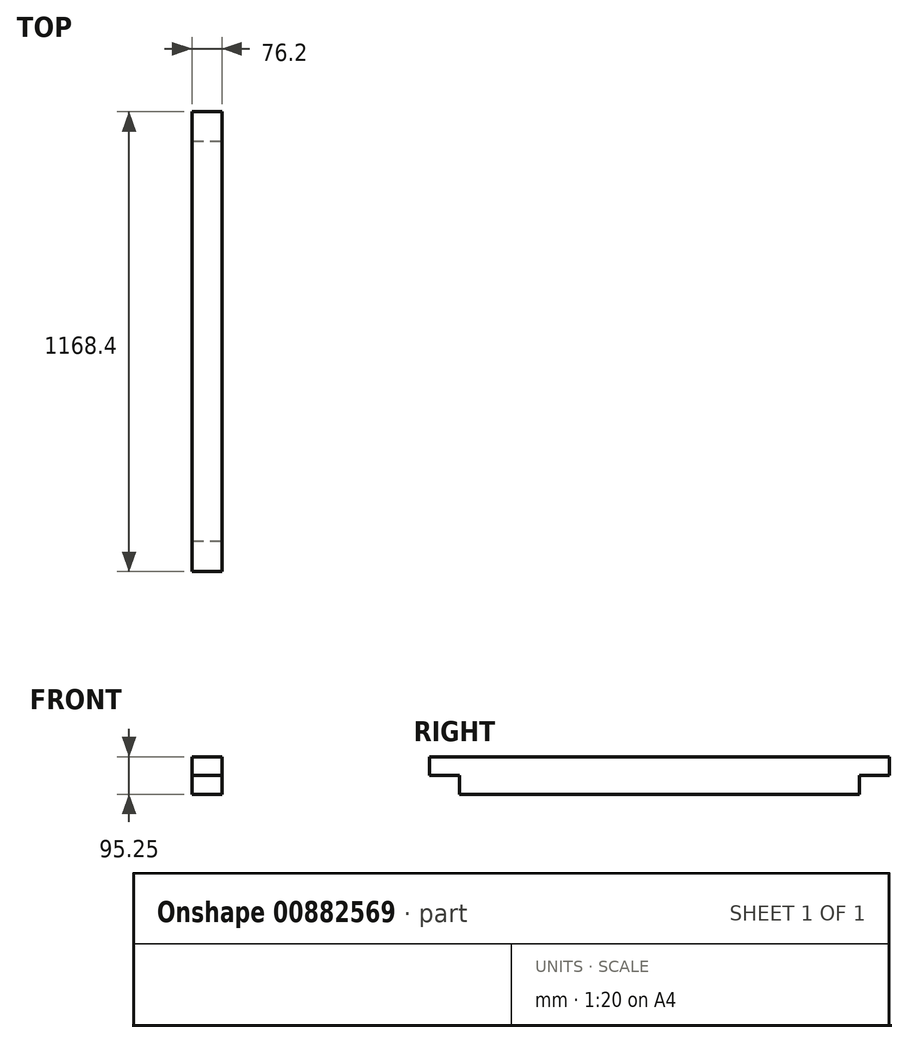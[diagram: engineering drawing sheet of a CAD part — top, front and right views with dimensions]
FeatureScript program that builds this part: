
annotation { "Feature Type Name" : "Feature", "Feature Type Description" : "" }
export const myFeature = defineFeature(function(context is Context, id is Id, definition is map)
    precondition{}
    {
        {
            var Q0;
            Q0=qCreatedBy(makeId("Front.planeOp"),FACE);
            var sketch = newSketch(context, id + "F0", { "sketchPlane" : qUnion([Q0])});
            skLineSegment(sketch, "E0.bottom", {"start": v(0, 0) * mm, "end": v(76.2, 0) * mm});
            skLineSegment(sketch, "E0.top", {"start": v(0, 95.25) * mm, "end": v(76.2, 95.25) * mm});
            skLineSegment(sketch, "E0.left", {"start": v(0, 0) * mm, "end": v(0, 95.25) * mm});
            skLineSegment(sketch, "E0.right", {"start": v(76.2, 0) * mm, "end": v(76.2, 95.25) * mm});
            skSolve(sketch);
        }
        {
            var Q0;
            Q0 = qSketchRegion(id + "F0", true);
            extrude(context, id + "F1", {"entities" : qUnion([Q0]), "depth" : 1168.4 * mm, "offsetDistance" : 25.4 * mm});
        }
        {
            var Q0;
            Q0=makeQuery(id+"F1.opExtrude","SWEPT_FACE",FACE,{"disambiguationData":[OSD([sQuery(id+"F0.wireOp",EDGE,"E0.bottom")])]});
            var sketch = newSketch(context, id + "F2", { "sketchPlane" : qUnion([Q0])});
            skLineSegment(sketch, "E1.bottom", {"start": v(76.2, 0) * mm, "end": v(0, 0) * mm});
            skLineSegment(sketch, "E1.top", {"start": v(76.2, 76.2) * mm, "end": v(0, 76.2) * mm});
            skLineSegment(sketch, "E1.left", {"start": v(76.2, 0) * mm, "end": v(76.2, 76.2) * mm});
            skLineSegment(sketch, "E1.right", {"start": v(0, 0) * mm, "end": v(0, 76.2) * mm});
            skLineSegment(sketch, "E2.bottom", {"start": v(76.2, 1168.4) * mm, "end": v(0, 1168.4) * mm});
            skLineSegment(sketch, "E2.top", {"start": v(76.2, 1092.2) * mm, "end": v(0, 1092.2) * mm});
            skLineSegment(sketch, "E2.left", {"start": v(76.2, 1168.4) * mm, "end": v(76.2, 1092.2) * mm});
            skLineSegment(sketch, "E2.right", {"start": v(0, 1168.4) * mm, "end": v(0, 1092.2) * mm});
            skSolve(sketch);
        }
        {
            var Q0;
            Q0 = qSketchRegion(id + "F2", true);
            extrude(context, id + "F3", {"entities" : qUnion([Q0]), "operationType" : NewBodyOperationType.REMOVE, "oppositeDirection" : true, "depth" : 47.62 * mm, "offsetDistance" : 25.4 * mm});
        }
    });
